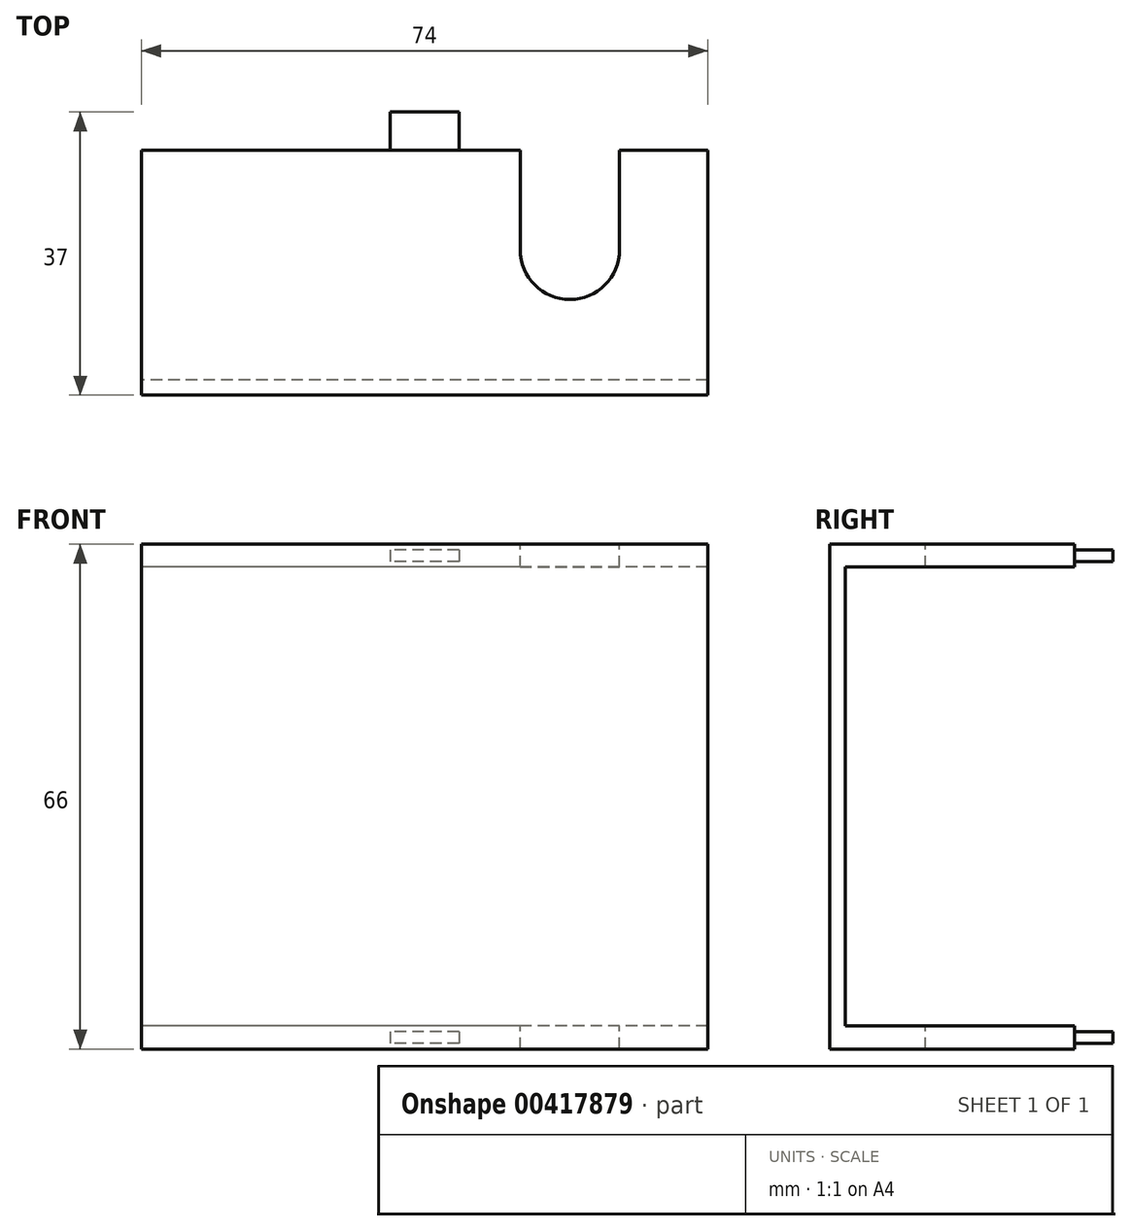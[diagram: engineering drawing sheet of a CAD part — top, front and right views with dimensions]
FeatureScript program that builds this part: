
annotation { "Feature Type Name" : "Feature", "Feature Type Description" : "" }
export const myFeature = defineFeature(function(context is Context, id is Id, definition is map)
    precondition{}
    {
        {
            var Q0;
            Q0=qCreatedBy(makeId("Top.planeOp"),FACE);
            var sketch = newSketch(context, id + "F0", { "sketchPlane" : qUnion([Q0])});
            skLineSegment(sketch, "E0.bottom", {"start": v(37, 16) * mm, "end": v(-37, 16) * mm});
            skLineSegment(sketch, "E0.top", {"start": v(37, -16) * mm, "end": v(-37, -16) * mm});
            skLineSegment(sketch, "E0.left", {"start": v(37, 16) * mm, "end": v(37, -16) * mm});
            skLineSegment(sketch, "E0.right", {"start": v(-37, 16) * mm, "end": v(-37, -16) * mm});
            skPoint(sketch, "E0.middle", {"position": v(0, 0) * mm});
            skSolve(sketch);
        }
        {
            var Q0;
            Q0 = qSketchRegion(id + "F0", true);
            extrude(context, id + "F1", {"entities" : qUnion([Q0]), "depth" : 3 * mm});
        }
        {
            var Q0;
            Q0=makeQuery(id+"F1.opExtrude","CAP_FACE",FACE,{"disambiguationData":[OSD([sQuery(id+"F0.wireOp",EDGE,"E0.bottom"),sQuery(id+"F0.wireOp",EDGE,"E0.top"),sQuery(id+"F0.wireOp",EDGE,"E0.left"),sQuery(id+"F0.wireOp",EDGE,"E0.right")])],"isStart":true});
            var sketch = newSketch(context, id + "F2", { "sketchPlane" : qUnion([Q0])});
            skLineSegment(sketch, "E1.bottom", {"start": v(37, 16) * mm, "end": v(-37, 16) * mm});
            skLineSegment(sketch, "E1.top", {"start": v(37, 14) * mm, "end": v(-37, 14) * mm});
            skLineSegment(sketch, "E1.left", {"start": v(37, 16) * mm, "end": v(37, 14) * mm});
            skLineSegment(sketch, "E1.right", {"start": v(-37, 16) * mm, "end": v(-37, 14) * mm});
            skSolve(sketch);
        }
        {
            var Q0;
            Q0 = qSketchRegion(id + "F2", true);
            extrude(context, id + "F3", {"entities" : qUnion([Q0]), "operationType" : NewBodyOperationType.ADD, "depth" : 60 * mm});
        }
        {
            var Q0;
            Q0=makeQuery(id+"F3.opExtrude","CAP_FACE",FACE,{"disambiguationData":[OSD([sQuery(id+"F2.wireOp",EDGE,"E1.bottom"),sQuery(id+"F2.wireOp",EDGE,"E1.top"),sQuery(id+"F2.wireOp",EDGE,"E1.left"),sQuery(id+"F2.wireOp",EDGE,"E1.right")])],"isStart":false});
            var sketch = newSketch(context, id + "F4", { "sketchPlane" : qUnion([Q0])});
            skLineSegment(sketch, "E2.bottom", {"start": v(37, 16) * mm, "end": v(-37, 16) * mm});
            skLineSegment(sketch, "E2.top", {"start": v(37, -16) * mm, "end": v(-37, -16) * mm});
            skLineSegment(sketch, "E2.left", {"start": v(37, 16) * mm, "end": v(37, -16) * mm});
            skLineSegment(sketch, "E2.right", {"start": v(-37, 16) * mm, "end": v(-37, -16) * mm});
            skSolve(sketch);
        }
        {
            var Q0;
            Q0 = qSketchRegion(id + "F4", true);
            extrude(context, id + "F5", {"entities" : qUnion([Q0]), "operationType" : NewBodyOperationType.ADD, "depth" : 3 * mm});
        }
        {
            var Q0;
            Q0=makeQuery(id+"F1.opExtrude","SWEPT_FACE",FACE,{"disambiguationData":[OSD([sQuery(id+"F0.wireOp",EDGE,"E0.bottom")])]});
            var sketch = newSketch(context, id + "F6", { "sketchPlane" : qUnion([Q0])});
            skLineSegment(sketch, "E3.bottom", {"start": v(-4.5, 2.25) * mm, "end": v(4.5, 2.25) * mm});
            skLineSegment(sketch, "E3.top", {"start": v(-4.5, 0.75) * mm, "end": v(4.5, 0.75) * mm});
            skLineSegment(sketch, "E3.left", {"start": v(-4.5, 2.25) * mm, "end": v(-4.5, 0.75) * mm});
            skLineSegment(sketch, "E3.right", {"start": v(4.5, 2.25) * mm, "end": v(4.5, 0.75) * mm});
            skPoint(sketch, "E3.middle", {"position": v(0, 1.5) * mm});
            skPoint(sketch, "E3.middle.positionSnap0", {"position": v(0, 3) * mm});
            skPoint(sketch, "E3.centerSnap0", {"position": v(0, 3) * mm});
            skSolve(sketch);
        }
        {
            var Q0;
            Q0 = qSketchRegion(id + "F6", true);
            extrude(context, id + "F7", {"entities" : qUnion([Q0]), "operationType" : NewBodyOperationType.ADD, "depth" : 5 * mm});
        }
        {
            var Q0;
            Q0=makeQuery(id+"F5.opExtrude","SWEPT_FACE",FACE,{"disambiguationData":[OSD([sQuery(id+"F4.wireOp",EDGE,"E2.top")])]});
            var sketch = newSketch(context, id + "F8", { "sketchPlane" : qUnion([Q0])});
            skLineSegment(sketch, "E4.bottom", {"start": v(-4.5, -60.75) * mm, "end": v(4.5, -60.75) * mm});
            skLineSegment(sketch, "E4.top", {"start": v(-4.5, -62.25) * mm, "end": v(4.5, -62.25) * mm});
            skLineSegment(sketch, "E4.left", {"start": v(-4.5, -60.75) * mm, "end": v(-4.5, -62.25) * mm});
            skLineSegment(sketch, "E4.right", {"start": v(4.5, -60.75) * mm, "end": v(4.5, -62.25) * mm});
            skPoint(sketch, "E4.middle", {"position": v(0, -61.5) * mm});
            skPoint(sketch, "E4.middle.positionSnap0", {"position": v(0, -60) * mm});
            skPoint(sketch, "E4.centerSnap0", {"position": v(0, -60) * mm});
            skSolve(sketch);
        }
        {
            var Q0;
            Q0 = qSketchRegion(id + "F8", true);
            extrude(context, id + "F9", {"entities" : qUnion([Q0]), "operationType" : NewBodyOperationType.ADD, "depth" : 5 * mm});
        }
        {
            var Q0;
            Q0=makeQuery(id+"F1.opExtrude","CAP_FACE",FACE,{"disambiguationData":[OSD([sQuery(id+"F0.wireOp",EDGE,"E0.bottom"),sQuery(id+"F0.wireOp",EDGE,"E0.top"),sQuery(id+"F0.wireOp",EDGE,"E0.left"),sQuery(id+"F0.wireOp",EDGE,"E0.right")])],"isStart":false});
            var sketch = newSketch(context, id + "F10", { "sketchPlane" : qUnion([Q0])});
            skArc(sketch, "E5", {"start": v(12.5, 3) * mm, "mid": v(19, -3.5) * mm, "end": v(25.5, 3) * mm});
            skLineSegment(sketch, "E6", {"start": v(12.5, 3) * mm, "end": v(12.5, 16) * mm});
            skLineSegment(sketch, "E7", {"start": v(25.5, 3) * mm, "end": v(25.5, 16) * mm});
            skLineSegment(sketch, "E8", {"start": v(25.5, 16) * mm, "end": v(12.5, 16) * mm});
            skSolve(sketch);
        }
        {
            var Q0;
            Q0 = qSketchRegion(id + "F10", true);
            var Q1;
            Q1=makeQuery(id+"F5.opExtrude","CAP_FACE",FACE,{"disambiguationData":[OSD([sQuery(id+"F4.wireOp",EDGE,"E2.bottom"),sQuery(id+"F4.wireOp",EDGE,"E2.top"),sQuery(id+"F4.wireOp",EDGE,"E2.left"),sQuery(id+"F4.wireOp",EDGE,"E2.right")])],"isStart":false});
            extrude(context, id + "F11", {"entities" : qUnion([Q0]), "operationType" : NewBodyOperationType.REMOVE, "endBound" : BoundingType.UP_TO_SURFACE, "oppositeDirection" : true, "endBoundEntityFace" : qUnion([Q1]), "depth" : 25 * mm});
        }
    });
